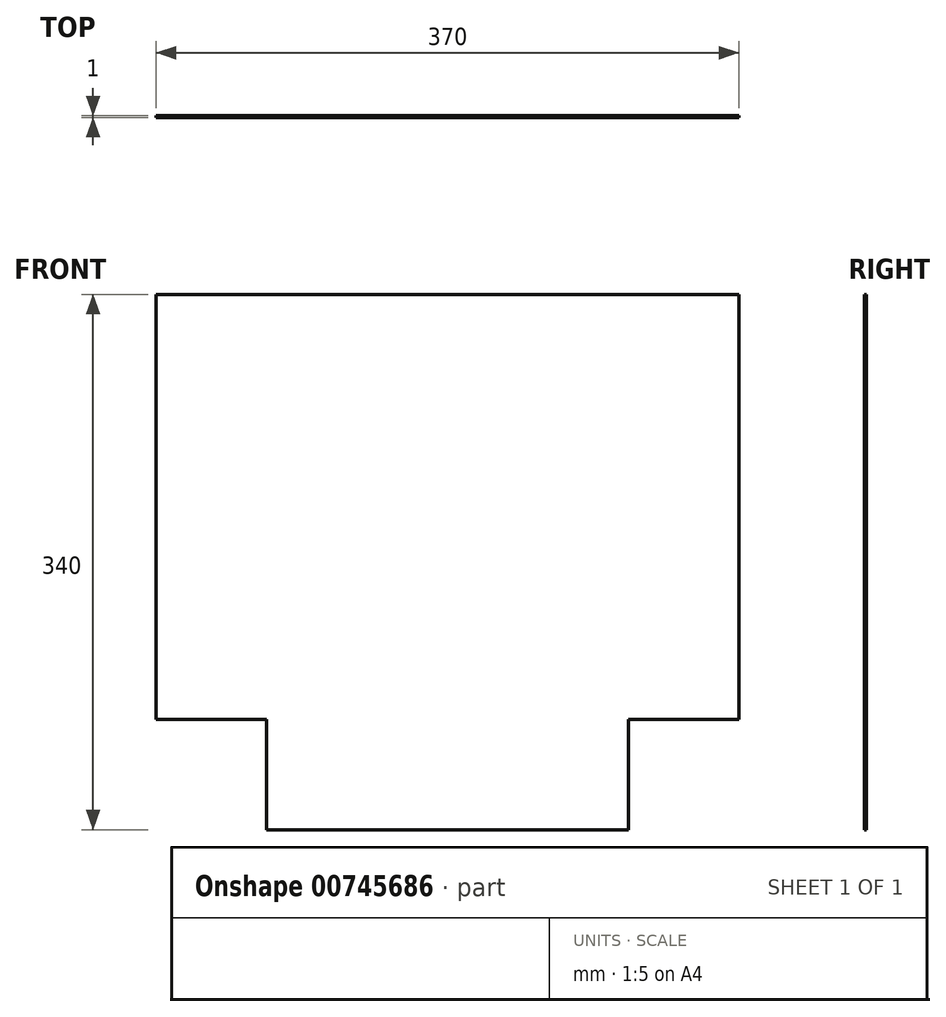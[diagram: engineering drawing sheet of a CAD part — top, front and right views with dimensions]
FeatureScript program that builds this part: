
annotation { "Feature Type Name" : "Feature", "Feature Type Description" : "" }
export const myFeature = defineFeature(function(context is Context, id is Id, definition is map)
    precondition{}
    {
        {
            var Q0;
            Q0=qCreatedBy(makeId("Front.planeOp"),FACE);
            var sketch = newSketch(context, id + "F0", { "sketchPlane" : qUnion([Q0])});
            skPoint(sketch, "E0.middle", {"position": v(0, 0) * mm});
            skLineSegment(sketch, "E1.bottom", {"start": v(-115, -115) * mm, "end": v(-185, -115) * mm});
            skLineSegment(sketch, "E1.top", {"start": v(-115, 155) * mm, "end": v(-185, 155) * mm});
            skLineSegment(sketch, "E1.right", {"start": v(-185, -115) * mm, "end": v(-185, 155) * mm});
            skLineSegment(sketch, "E2.bottom", {"start": v(115, -115) * mm, "end": v(185, -115) * mm});
            skLineSegment(sketch, "E2.top", {"start": v(115, 155) * mm, "end": v(185, 155) * mm});
            skLineSegment(sketch, "E2.right", {"start": v(185, -115) * mm, "end": v(185, 155) * mm});
            skLineSegment(sketch, "E3.top", {"start": v(-115, -185) * mm, "end": v(115, -185) * mm});
            skLineSegment(sketch, "E3.left", {"start": v(-115, -115) * mm, "end": v(-115, -185) * mm});
            skLineSegment(sketch, "E3.right", {"start": v(115, -115) * mm, "end": v(115, -185) * mm});
            skLineSegment(sketch, "E4", {"start": v(-115, 155) * mm, "end": v(115, 155) * mm});
            skSolve(sketch);
        }
        {
            var Q0;
            Q0 = qSketchRegion(id + "F0", true);
            extrude(context, id + "F1", {"entities" : qUnion([Q0]), "depth" : 1 * mm, "offsetDistance" : 25.4 * mm});
        }
    });
